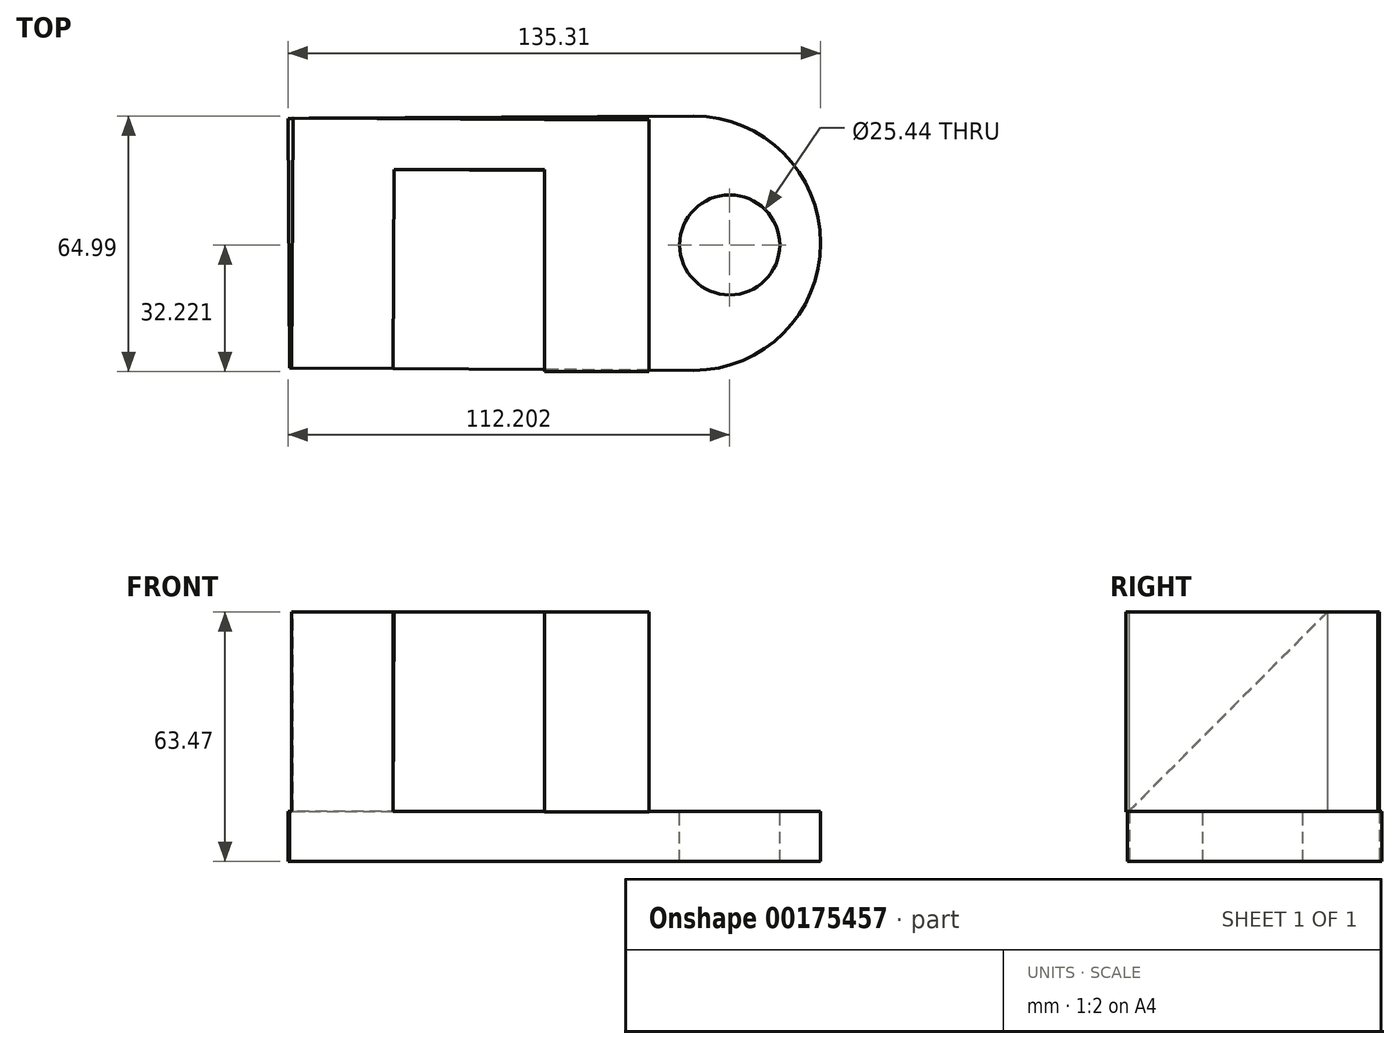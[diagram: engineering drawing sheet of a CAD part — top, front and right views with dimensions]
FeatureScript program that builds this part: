
annotation { "Feature Type Name" : "Feature", "Feature Type Description" : "" }
export const myFeature = defineFeature(function(context is Context, id is Id, definition is map)
    precondition{}
    {
        {
            var Q0;
            Q0=qCreatedBy(makeId("Top.planeOp"),FACE);
            var sketch = newSketch(context, id + "F0", { "sketchPlane" : qUnion([Q0])});
            skArc(sketch, "E0", {"start": v(-28.08, -31.67) * mm, "mid": v(-58.93, 1.22) * mm, "end": v(-25.64, 31.64) * mm});
            skArc(sketch, "E1", {"start": v(87.15, -32.33) * mm, "mid": v(119.48, 0) * mm, "end": v(87.15, 32.33) * mm});
            skLineSegment(sketch, "E2", {"start": v(-25.64, 31.64) * mm, "end": v(87.15, 32.33) * mm});
            skLineSegment(sketch, "E3", {"start": v(87.15, -32.33) * mm, "end": v(-28.08, -31.67) * mm});
            skLineSegment(sketch, "E4", {"start": v(-28.08, -31.67) * mm, "end": v(-15.44, -31.74) * mm});
            skLineSegment(sketch, "E5", {"start": v(-15.44, -31.74) * mm, "end": v(-15.83, 31.7) * mm});
            skLineSegment(sketch, "E6", {"start": v(87.15, -32.33) * mm, "end": v(74.1, -32.26) * mm});
            skLineSegment(sketch, "E7", {"start": v(74.1, -32.26) * mm, "end": v(73.7, 32.25) * mm});
            skLineSegment(sketch, "E8", {"start": v(73.7, 32.25) * mm, "end": v(-15.83, 31.7) * mm});
            skLineSegment(sketch, "E9", {"start": v(-15.44, -31.74) * mm, "end": v(10.34, -31.9) * mm});
            skLineSegment(sketch, "E10", {"start": v(10.34, -31.9) * mm, "end": v(10.03, 18.89) * mm});
            skLineSegment(sketch, "E11", {"start": v(10.03, 18.89) * mm, "end": v(45.62, 18.68) * mm});
            skLineSegment(sketch, "E12", {"start": v(45.62, 18.68) * mm, "end": v(45.93, -31.74) * mm});
            skSolve(sketch);
        }
        {
            var Q0;
            {var subQ0=sQuery(id+"F0.wireOp",EDGE,"E0");Q0=makeQuery(id+"F0.imprint","IMPRINT",FACE,{"disambiguationData":[TD([[makeQuery(id+"F0.imprint","IMPRINT",EDGE,{"derivedFrom":subQ0}),-1.0]])]});}
            var Q1;
            {var subQ0=sQuery(id+"F0.wireOp",EDGE,"E1");Q1=makeQuery(id+"F0.imprint","IMPRINT",FACE,{"disambiguationData":[TD([[makeQuery(id+"F0.imprint","IMPRINT",EDGE,{"derivedFrom":subQ0}),1.0]])]});}
            var Q2;
            Q2=makeQuery(id+"F0.imprint","IMPRINT",FACE,{"disambiguationData":[TD([[makeQuery(id+"F0.imprint","IMPRINT",EDGE,{"derivedFrom":sQuery(id+"F0.wireOp",EDGE,"E3")}),-1.0]])]});
            extrude(context, id + "F1", {"entities" : qUnion([Q0, Q1, Q2]), "depth" : 12.7 * mm});
        }
        {
            var Q0;
            Q0=makeQuery(id+"F1.opExtrude","SWEPT_FACE",FACE,{"disambiguationData":[OSD([sQuery(id+"F0.wireOp",EDGE,"E3"),sQuery(id+"F0.wireOp",EDGE,"E4"),sQuery(id+"F0.wireOp",EDGE,"E6"),sQuery(id+"F0.wireOp",EDGE,"E9")])]});
            var sketch = newSketch(context, id + "F2", { "sketchPlane" : qUnion([Q0])});
            skLineSegment(sketch, "E13", {"start": v(-14.69, 12.7) * mm, "end": v(-14.69, 63.47) * mm});
            skLineSegment(sketch, "E14", {"start": v(-14.69, 63.47) * mm, "end": v(10.98, 63.47) * mm});
            skLineSegment(sketch, "E15", {"start": v(10.98, 63.47) * mm, "end": v(10.98, 12.7) * mm});
            skLineSegment(sketch, "E16", {"start": v(-14.69, 63.47) * mm, "end": v(-14.69, 12.7) * mm});
            skLineSegment(sketch, "E17", {"start": v(-14.69, 12.7) * mm, "end": v(10.98, 12.7) * mm});
            skSolve(sketch);
        }
        {
            var Q0;
            Q0 = qSketchRegion(id + "F2", true);
            extrude(context, id + "F3", {"entities" : qUnion([Q0]), "operationType" : NewBodyOperationType.ADD, "oppositeDirection" : true, "depth" : 63.5 * mm});
        }
        {
            var Q0;
            Q0=makeQuery(id+"F3.opExtrude","SWEPT_FACE",FACE,{"disambiguationData":[OSD([sQuery(id+"F2.wireOp",EDGE,"E14")])]});
            var sketch = newSketch(context, id + "F4", { "sketchPlane" : qUnion([Q0])});
            skLineSegment(sketch, "E18", {"start": v(11.16, 31.6) * mm, "end": v(49.31, 31.39) * mm});
            skLineSegment(sketch, "E19", {"start": v(49.31, 31.39) * mm, "end": v(49.31, 18.68) * mm});
            skLineSegment(sketch, "E20", {"start": v(49.31, 18.68) * mm, "end": v(11.09, 18.68) * mm});
            skLineSegment(sketch, "E21", {"start": v(11.09, 18.68) * mm, "end": v(11.16, 31.6) * mm});
            skLineSegment(sketch, "E22", {"start": v(49.31, 31.39) * mm, "end": v(11.16, 31.6) * mm});
            skSolve(sketch);
        }
        {
            var Q0;
            Q0 = qSketchRegion(id + "F4", true);
            extrude(context, id + "F5", {"entities" : qUnion([Q0]), "operationType" : NewBodyOperationType.ADD, "endBound" : BoundingType.UP_TO_NEXT, "oppositeDirection" : true, "depth" : 25.4 * mm});
        }
        {
            var Q0;
            Q0=makeQuery(id+"F5.boolean.opBoolean","MERGE",FACE,{"derivedFrom":[makeQuery(id+"F3.opExtrude","SWEPT_FACE",FACE,{"disambiguationData":[OSD([sQuery(id+"F2.wireOp",EDGE,"E14")])]}),makeQuery(id+"F5.opExtrude","CAP_FACE",FACE,{"disambiguationData":[OSD([sQuery(id+"F4.wireOp",EDGE,"E19"),sQuery(id+"F4.wireOp",EDGE,"E20"),sQuery(id+"F4.wireOp",EDGE,"E21"),sQuery(id+"F4.wireOp",EDGE,"E22")])],"isStart":true})]});
            var sketch = newSketch(context, id + "F6", { "sketchPlane" : qUnion([Q0])});
            skLineSegment(sketch, "E23.bottom", {"start": v(49.31, 31.39) * mm, "end": v(75.83, 31.39) * mm});
            skLineSegment(sketch, "E23.top", {"start": v(49.31, -32.66) * mm, "end": v(75.83, -32.66) * mm});
            skLineSegment(sketch, "E23.left", {"start": v(49.31, 31.39) * mm, "end": v(49.31, -32.66) * mm});
            skLineSegment(sketch, "E23.right", {"start": v(75.83, 31.39) * mm, "end": v(75.83, -32.66) * mm});
            skSolve(sketch);
        }
        {
            var Q0;
            Q0 = qSketchRegion(id + "F6", true);
            extrude(context, id + "F7", {"entities" : qUnion([Q0]), "operationType" : NewBodyOperationType.ADD, "oppositeDirection" : true, "depth" : 50.8 * mm});
        }
        {
            var Q0;
            Q0=makeQuery(id+"F3.opExtrude","SWEPT_FACE",FACE,{"disambiguationData":[OSD([sQuery(id+"F2.wireOp",EDGE,"E15")])]});
            var sketch = newSketch(context, id + "F8", { "sketchPlane" : qUnion([Q0])});
            skLineSegment(sketch, "E24", {"start": v(18.75, 63.47) * mm, "end": v(-31.83, 12.7) * mm});
            skLineSegment(sketch, "E25", {"start": v(-31.83, 12.7) * mm, "end": v(18.75, 12.7) * mm});
            skLineSegment(sketch, "E26", {"start": v(18.75, 12.7) * mm, "end": v(18.75, 63.47) * mm});
            skSolve(sketch);
        }
        {
            var Q0;
            Q0 = qSketchRegion(id + "F8", true);
            extrude(context, id + "F9", {"entities" : qUnion([Q0]), "operationType" : NewBodyOperationType.ADD, "endBound" : BoundingType.UP_TO_NEXT, "depth" : 25.4 * mm});
        }
        {
            var Q0;
            Q0=makeQuery(id+"F7.boolean.opBoolean","MERGE",FACE,{"derivedFrom":[makeQuery(id+"F5.boolean.opBoolean","MERGE",FACE,{"derivedFrom":[makeQuery(id+"F3.opExtrude","SWEPT_FACE",FACE,{"disambiguationData":[OSD([sQuery(id+"F2.wireOp",EDGE,"E14")])]}),makeQuery(id+"F5.opExtrude","CAP_FACE",FACE,{"disambiguationData":[OSD([sQuery(id+"F4.wireOp",EDGE,"E19"),sQuery(id+"F4.wireOp",EDGE,"E20"),sQuery(id+"F4.wireOp",EDGE,"E21"),sQuery(id+"F4.wireOp",EDGE,"E22")])],"isStart":true})]}),makeQuery(id+"F7.opExtrude","CAP_FACE",FACE,{"disambiguationData":[OSD([sQuery(id+"F6.wireOp",EDGE,"E23.bottom"),sQuery(id+"F6.wireOp",EDGE,"E23.top"),sQuery(id+"F6.wireOp",EDGE,"E23.left"),sQuery(id+"F6.wireOp",EDGE,"E23.right")])],"isStart":true})]});
            var sketch = newSketch(context, id + "F10", { "sketchPlane" : qUnion([Q0])});
            skCircle(sketch, "E27", {"center": v(-32.27, 0) * mm, "radius": 12.77 * mm});
            skSolve(sketch);
        }
        {
            var Q0;
            Q0 = qSketchRegion(id + "F10", true);
            extrude(context, id + "F11", {"entities" : qUnion([Q0]), "operationType" : NewBodyOperationType.REMOVE, "endBound" : BoundingType.THROUGH_ALL, "oppositeDirection" : true, "depth" : 25.4 * mm});
        }
        {
            var Q0;
            {var subQ5=sQuery(id+"F0.wireOp",EDGE,"E8");var subQ6=sQuery(id+"F0.wireOp",EDGE,"E2");var subQ8=sQuery(id+"F0.wireOp",EDGE,"E9");var subQ9=sQuery(id+"F0.wireOp",EDGE,"E6");var subQ10=sQuery(id+"F0.wireOp",EDGE,"E4");var subQ11=sQuery(id+"F0.wireOp",EDGE,"E3");var subQ13=sQuery(id+"F0.wireOp",EDGE,"E1");var subQ14=makeQuery(id+"F1.opExtrude","SWEPT_FACE",FACE,{"disambiguationData":[OSD([subQ13])]});Q0=makeQuery(id+"F7.boolean.opBoolean","SPLIT",FACE,{"disambiguationData":[TD([subQ14])],"derivedFrom":makeQuery(id+"F3.boolean.opBoolean","SPLIT",FACE,{"disambiguationData":[TD([subQ14])],"derivedFrom":makeQuery(id+"F1.opExtrude","CAP_FACE",FACE,{"disambiguationData":[OSD([sQuery(id+"F0.wireOp",EDGE,"E0"),subQ13,subQ6,subQ11,subQ10,subQ9,subQ5,subQ8])],"isStart":false})})});}
            var sketch = newSketch(context, id + "F12", { "sketchPlane" : qUnion([Q0])});
            skCircle(sketch, "E28", {"center": v(96.37, -0.44) * mm, "radius": 12.72 * mm});
            skPoint(sketch, "E28.centerSnap0", {"position": v(75.83, -0.44) * mm});
            skSolve(sketch);
        }
        {
            var Q0;
            Q0 = qSketchRegion(id + "F12", true);
            extrude(context, id + "F13", {"entities" : qUnion([Q0]), "operationType" : NewBodyOperationType.REMOVE, "endBound" : BoundingType.THROUGH_ALL, "oppositeDirection" : true, "depth" : 25.4 * mm});
        }
    });
